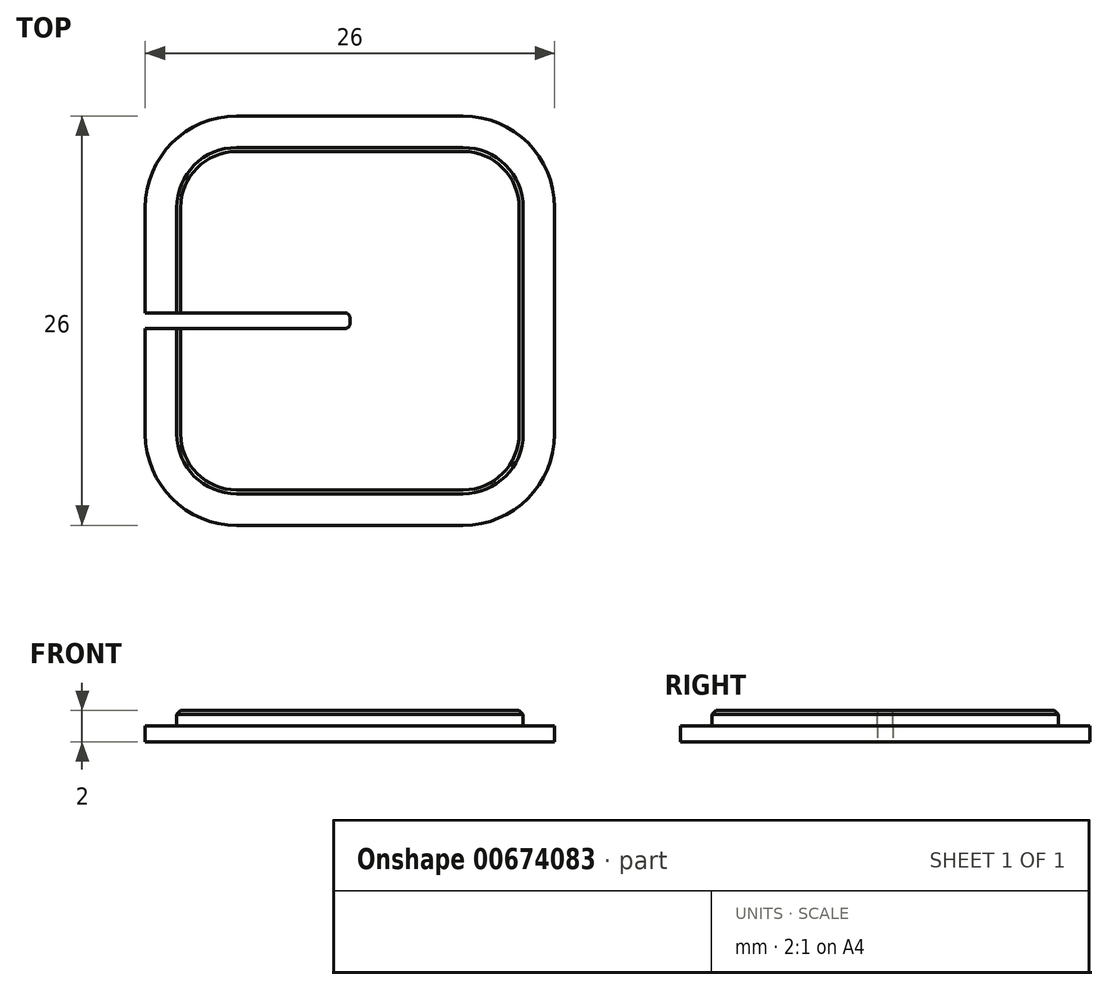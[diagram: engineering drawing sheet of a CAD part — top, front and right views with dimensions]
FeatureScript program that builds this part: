
annotation { "Feature Type Name" : "Feature", "Feature Type Description" : "" }
export const myFeature = defineFeature(function(context is Context, id is Id, definition is map)
    precondition{}
    {
        {
            var Q0;
            Q0=qCreatedBy(makeId("Top.planeOp"),FACE);
            var sketch = newSketch(context, id + "F0", { "sketchPlane" : qUnion([Q0])});
            skCircle(sketch, "E0.cCircle", {"center": v(0, 0) * mm, "radius": 11 * mm, "construction": true});
            skLineSegment(sketch, "E0.0", {"start": v(-7.2, 11) * mm, "end": v(7.2, 11) * mm});
            skLineSegment(sketch, "E0.1", {"start": v(11, 7.2) * mm, "end": v(11, -7.2) * mm});
            skLineSegment(sketch, "E0.2", {"start": v(7.2, -11) * mm, "end": v(-7.2, -11) * mm});
            skLineSegment(sketch, "E0.3", {"start": v(-11, -7.2) * mm, "end": v(-11, 7.2) * mm});
            skPoint(sketch, "E0.0.midPoint", {"position": v(0, 11) * mm});
            skPoint(sketch, "E1.visualSharp", {"position": v(-11, 11) * mm});
            skArc(sketch, "E1.filletArc", {"start": v(-7.2, 11) * mm, "mid": v(-9.88, 9.88) * mm, "end": v(-11, 7.2) * mm});
            skPoint(sketch, "E2.visualSharp", {"position": v(11, 11) * mm});
            skArc(sketch, "E2.filletArc", {"start": v(11, 7.2) * mm, "mid": v(9.88, 9.88) * mm, "end": v(7.2, 11) * mm});
            skPoint(sketch, "E3.visualSharp", {"position": v(11, -11) * mm});
            skArc(sketch, "E3.filletArc", {"start": v(7.2, -11) * mm, "mid": v(9.88, -9.88) * mm, "end": v(11, -7.2) * mm});
            skPoint(sketch, "E4.visualSharp", {"position": v(-11, -11) * mm});
            skArc(sketch, "E4.filletArc", {"start": v(-11, -7.2) * mm, "mid": v(-9.88, -9.88) * mm, "end": v(-7.2, -11) * mm});
            skLineSegment(sketch, "E5.0", {"start": v(13, 7.2) * mm, "end": v(13, -7.2) * mm});
            skArc(sketch, "E5.1", {"start": v(7.2, -13) * mm, "mid": v(11.3, -11.3) * mm, "end": v(13, -7.2) * mm});
            skArc(sketch, "E5.2", {"start": v(13, 7.2) * mm, "mid": v(11.3, 11.3) * mm, "end": v(7.2, 13) * mm});
            skLineSegment(sketch, "E5.3", {"start": v(7.2, -13) * mm, "end": v(-7.2, -13) * mm});
            skLineSegment(sketch, "E5.4", {"start": v(-7.2, 13) * mm, "end": v(7.2, 13) * mm});
            skArc(sketch, "E5.5", {"start": v(-7.2, 13) * mm, "mid": v(-11.3, 11.3) * mm, "end": v(-13, 7.2) * mm});
            skLineSegment(sketch, "E5.6", {"start": v(-13, -7.2) * mm, "end": v(-13, 7.2) * mm});
            skArc(sketch, "E5.7", {"start": v(-13, -7.2) * mm, "mid": v(-11.3, -11.3) * mm, "end": v(-7.2, -13) * mm});
            skSolve(sketch);
        }
        {
            var Q0;
            Q0=makeQuery(id+"F0.imprint","IMPRINT",FACE,{"disambiguationData":[TD([[makeQuery(id+"F0.imprint","IMPRINT",EDGE,{"derivedFrom":sQuery(id+"F0.wireOp",EDGE,"E0.0")}),1.0]])]});
            extrude(context, id + "F1", {"entities" : qUnion([Q0]), "depth" : 1 * mm, "offsetDistance" : 25.4 * mm});
        }
        {
            var Q0;
            Q0=makeQuery(id+"F0.imprint","IMPRINT",FACE,{"disambiguationData":[TD([[makeQuery(id+"F0.imprint","IMPRINT",EDGE,{"derivedFrom":sQuery(id+"F0.wireOp",EDGE,"E0.0")}),-1.0]])]});
            extrude(context, id + "F2", {"entities" : qUnion([Q0]), "operationType" : NewBodyOperationType.ADD, "depth" : 2 * mm, "offsetDistance" : 25.4 * mm});
        }
        {
            var Q0;
            Q0=makeQuery(id+"F0.imprint","IMPRINT",FACE,{"disambiguationData":[TD([[makeQuery(id+"F0.imprint","IMPRINT",EDGE,{"derivedFrom":sQuery(id+"F0.wireOp",EDGE,"E0.0")}),-1.0]])]});
            var sketch = newSketch(context, id + "F3", { "sketchPlane" : qUnion([Q0])});
            skLineSegment(sketch, "E6.bottom", {"start": v(0, 0) * mm, "end": v(-13, 0) * mm});
            skLineSegment(sketch, "E6.top", {"start": v(0, -0.5) * mm, "end": v(-13, -0.5) * mm});
            skLineSegment(sketch, "E6.left", {"start": v(0, 0) * mm, "end": v(0, -0.5) * mm});
            skLineSegment(sketch, "E6.right", {"start": v(-13, 0) * mm, "end": v(-13, -0.5) * mm});
            skLineSegment(sketch, "E7.MirrorCS", {"start": v(0, 0.5) * mm, "end": v(-13, 0.5) * mm});
            skLineSegment(sketch, "E8.MirrorCS", {"start": v(0, 0) * mm, "end": v(0, 0.5) * mm});
            skLineSegment(sketch, "E9.MirrorCS", {"start": v(-13, 0) * mm, "end": v(-13, 0.5) * mm});
            skSolve(sketch);
        }
        {
            var Q0;
            Q0 = qSketchRegion(id + "F3", true);
            extrude(context, id + "F4", {"entities" : qUnion([Q0]), "operationType" : NewBodyOperationType.REMOVE, "depth" : 25.4 * mm, "offsetDistance" : 25.4 * mm});
        }
        {
            var Q0;
            {var subQ0=sQuery(id+"F0.wireOp",EDGE,"E1.filletArc");var subQ1=sQuery(id+"F0.wireOp",EDGE,"E0.3");Q0=makeQuery(id+"F4.boolean.opBoolean","SPLIT",EDGE,{"disambiguationData":[TD([makeQuery(id+"F2.opExtrude","SWEPT_FACE",FACE,{"disambiguationData":[OSD([subQ0])]})])],"derivedFrom":makeQuery(id+"F2.opExtrude","CAP_EDGE",EDGE,{"disambiguationData":[OSD([subQ1])],"isStart":false})});}
            var Q1;
            Q1=makeQuery(id+"F2.opExtrude","CAP_EDGE",EDGE,{"disambiguationData":[OSD([sQuery(id+"F0.wireOp",EDGE,"E1.filletArc")])],"isStart":false});
            var Q2;
            Q2=makeQuery(id+"F2.opExtrude","CAP_EDGE",EDGE,{"disambiguationData":[OSD([sQuery(id+"F0.wireOp",EDGE,"E0.0")])],"isStart":false});
            var Q3;
            Q3=makeQuery(id+"F2.opExtrude","CAP_EDGE",EDGE,{"disambiguationData":[OSD([sQuery(id+"F0.wireOp",EDGE,"E0.1")])],"isStart":false});
            var Q4;
            Q4=makeQuery(id+"F2.opExtrude","CAP_EDGE",EDGE,{"disambiguationData":[OSD([sQuery(id+"F0.wireOp",EDGE,"E3.filletArc")])],"isStart":false});
            var Q5;
            Q5=makeQuery(id+"F2.opExtrude","CAP_EDGE",EDGE,{"disambiguationData":[OSD([sQuery(id+"F0.wireOp",EDGE,"E0.2")])],"isStart":false});
            var Q6;
            Q6=makeQuery(id+"F2.opExtrude","CAP_EDGE",EDGE,{"disambiguationData":[OSD([sQuery(id+"F0.wireOp",EDGE,"E4.filletArc")])],"isStart":false});
            var Q7;
            {var subQ0=sQuery(id+"F0.wireOp",EDGE,"E4.filletArc");var subQ1=sQuery(id+"F0.wireOp",EDGE,"E0.3");Q7=makeQuery(id+"F4.boolean.opBoolean","SPLIT",EDGE,{"disambiguationData":[TD([makeQuery(id+"F2.opExtrude","SWEPT_FACE",FACE,{"disambiguationData":[OSD([subQ0])]})])],"derivedFrom":makeQuery(id+"F2.opExtrude","CAP_EDGE",EDGE,{"disambiguationData":[OSD([subQ1])],"isStart":false})});}
            var Q8;
            Q8=makeQuery(id+"F2.opExtrude","CAP_EDGE",EDGE,{"disambiguationData":[OSD([sQuery(id+"F0.wireOp",EDGE,"E2.filletArc")])],"isStart":false});
            chamfer(context, id + "F5", {"entities" : qUnion([Q0, Q1, Q2, Q3, Q4, Q5, Q6, Q7, Q8]), "width" : 0.25 * mm, "tangentPropagation" : true});
        }
        {
            var Q0;
            Q0=makeQuery(id+"F4.boolean.opBoolean","COPY",EDGE,{"derivedFrom":makeQuery(id+"F4.opExtrude","SWEPT_EDGE",EDGE,{"disambiguationData":[OSD([sQuery(id+"F3.wireOp",EDGE,"E6.top"),sQuery(id+"F3.wireOp",EDGE,"E6.left")])]})});
            var Q1;
            Q1=makeQuery(id+"F4.boolean.opBoolean","COPY",EDGE,{"derivedFrom":makeQuery(id+"F4.opExtrude","SWEPT_EDGE",EDGE,{"disambiguationData":[OSD([sQuery(id+"F3.wireOp",EDGE,"E7.MirrorCS"),sQuery(id+"F3.wireOp",EDGE,"E8.MirrorCS")])]})});
            fillet(context, id + "F6", {"entities" : qUnion([Q0, Q1]), "radius" : 0.32 * mm, "tangentPropagation" : true, "allowEdgeOverflow" : false});
        }
    });
